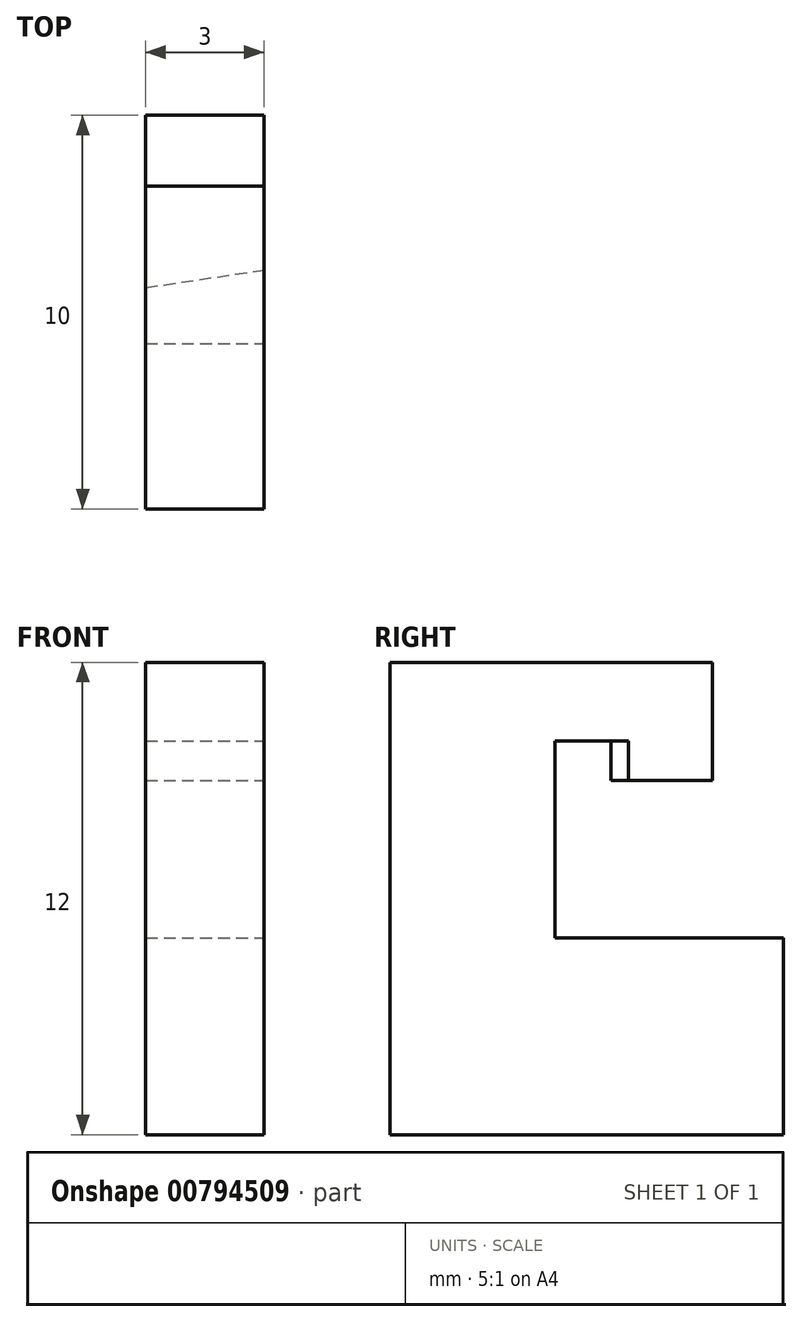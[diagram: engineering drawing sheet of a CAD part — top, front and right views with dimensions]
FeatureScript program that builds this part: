
annotation { "Feature Type Name" : "Feature", "Feature Type Description" : "" }
export const myFeature = defineFeature(function(context is Context, id is Id, definition is map)
    precondition{}
    {
        {
            var Q0;
            Q0=qCreatedBy(makeId("Top.planeOp"),FACE);
            var sketch = newSketch(context, id + "F0", { "sketchPlane" : qUnion([Q0])});
            skLineSegment(sketch, "E0.bottom", {"start": v(1.5, -5) * mm, "end": v(-1.5, -5) * mm});
            skLineSegment(sketch, "E0.top", {"start": v(1.5, 5) * mm, "end": v(-1.5, 5) * mm});
            skLineSegment(sketch, "E0.left", {"start": v(1.5, -5) * mm, "end": v(1.5, 5) * mm});
            skLineSegment(sketch, "E0.right", {"start": v(-1.5, -5) * mm, "end": v(-1.5, 5) * mm});
            skPoint(sketch, "E0.middle", {"position": v(0, 0) * mm});
            skSolve(sketch);
        }
        {
            var Q0;
            Q0=makeQuery(id+"F0.imprint","IMPRINT",FACE,{"disambiguationData":[TD([[makeQuery(id+"F0.imprint","IMPRINT",EDGE,{"derivedFrom":sQuery(id+"F0.wireOp",EDGE,"E0.bottom")}),-1.0]])]});
            extrude(context, id + "F1", {"entities" : qUnion([Q0]), "depth" : 5 * mm, "offsetDistance" : 25 * mm});
        }
        {
            var Q0;
            Q0=makeQuery(id+"F1.opExtrude","CAP_FACE",FACE,{"disambiguationData":[OSD([sQuery(id+"F0.wireOp",EDGE,"E0.bottom"),sQuery(id+"F0.wireOp",EDGE,"E0.top"),sQuery(id+"F0.wireOp",EDGE,"E0.left"),sQuery(id+"F0.wireOp",EDGE,"E0.right")])],"isStart":false});
            var sketch = newSketch(context, id + "F2", { "sketchPlane" : qUnion([Q0])});
            skLineSegment(sketch, "E1", {"start": v(-1.5, -0.8) * mm, "end": v(1.5, -0.8) * mm});
            skLineSegment(sketch, "E2", {"start": v(-5.57, -0.8) * mm, "end": v(-5.57, 5) * mm, "construction": true});
            skSolve(sketch);
        }
        {
            var Q0;
            {var subQ0=sQuery(id+"F2.wireOp",EDGE,"E1");Q0=makeQuery(id+"F2.imprint","IMPRINT",FACE,{"disambiguationData":[TD([[makeQuery(id+"F2.imprint","IMPRINT",EDGE,{"derivedFrom":subQ0}),-1.0]])]});}
            extrude(context, id + "F3", {"entities" : qUnion([Q0]), "operationType" : NewBodyOperationType.ADD, "depth" : 7 * mm, "offsetDistance" : 25 * mm});
        }
        {
            var Q0;
            Q0=makeQuery(id+"F3.opExtrude","SWEPT_FACE",FACE,{"disambiguationData":[OSD([sQuery(id+"F2.wireOp",EDGE,"E1")])]});
            var sketch = newSketch(context, id + "F4", { "sketchPlane" : qUnion([Q0])});
            skLineSegment(sketch, "E3", {"start": v(1.5, 10) * mm, "end": v(-1.5, 10) * mm});
            skLineSegment(sketch, "E4", {"start": v(5.91, 12) * mm, "end": v(5.91, 10) * mm, "construction": true});
            skSolve(sketch);
        }
        {
            var Q0;
            {var subQ0=sQuery(id+"F4.wireOp",EDGE,"E3");Q0=makeQuery(id+"F4.imprint","IMPRINT",FACE,{"disambiguationData":[TD([[makeQuery(id+"F4.imprint","IMPRINT",EDGE,{"derivedFrom":subQ0}),-1.0]])]});}
            extrude(context, id + "F5", {"entities" : qUnion([Q0]), "operationType" : NewBodyOperationType.ADD, "depth" : 4 * mm, "offsetDistance" : 25 * mm});
        }
        {
            var Q0;
            Q0=makeQuery(id+"F5.opExtrude","SWEPT_FACE",FACE,{"disambiguationData":[OSD([sQuery(id+"F4.wireOp",EDGE,"E3")])]});
            var sketch = newSketch(context, id + "F6", { "sketchPlane" : qUnion([Q0])});
            skLineSegment(sketch, "E5", {"start": v(-1.5, -0.62) * mm, "end": v(1.5, -1.07) * mm});
            skLineSegment(sketch, "E6", {"start": v(7.08, -1.9) * mm, "end": v(7.08, -3.2) * mm, "construction": true});
            skSolve(sketch);
        }
        {
            var Q0;
            {var subQ0=sQuery(id+"F6.wireOp",EDGE,"E5");Q0=makeQuery(id+"F6.imprint","IMPRINT",FACE,{"disambiguationData":[TD([[makeQuery(id+"F6.imprint","IMPRINT",EDGE,{"derivedFrom":subQ0}),-1.0]])]});}
            extrude(context, id + "F7", {"entities" : qUnion([Q0]), "operationType" : NewBodyOperationType.ADD, "depth" : 1 * mm, "offsetDistance" : 25 * mm});
        }
    });
